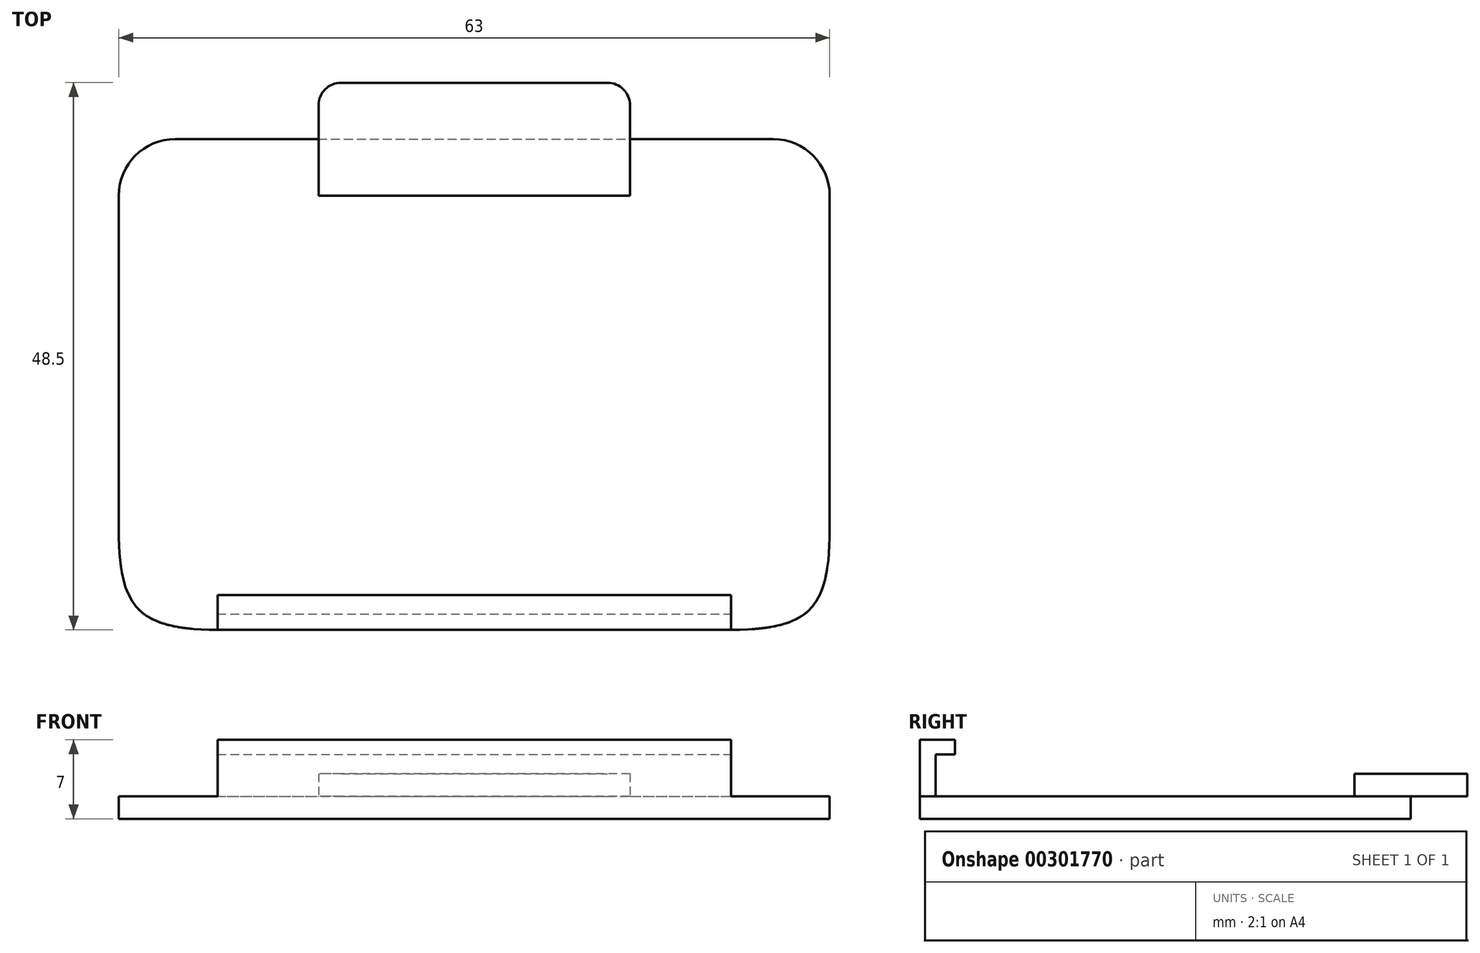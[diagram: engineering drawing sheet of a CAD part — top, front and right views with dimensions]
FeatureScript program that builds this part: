
annotation { "Feature Type Name" : "Feature", "Feature Type Description" : "" }
export const myFeature = defineFeature(function(context is Context, id is Id, definition is map)
    precondition{}
    {
        {
            var Q0;
            Q0=qCreatedBy(makeId("Top.planeOp"),FACE);
            var sketch = newSketch(context, id + "F0", { "sketchPlane" : qUnion([Q0])});
            skLineSegment(sketch, "E0.bottom", {"start": v(-7.54, 4.85) * mm, "end": v(55.46, 4.85) * mm});
            skLineSegment(sketch, "E0.top", {"start": v(-7.54, -38.65) * mm, "end": v(55.46, -38.65) * mm});
            skLineSegment(sketch, "E0.left", {"start": v(-7.54, 4.85) * mm, "end": v(-7.54, -38.65) * mm});
            skLineSegment(sketch, "E0.right", {"start": v(55.46, 4.85) * mm, "end": v(55.46, -38.65) * mm});
            skSolve(sketch);
        }
        {
            var Q0;
            Q0=makeQuery(id+"F0.imprint","IMPRINT",FACE,{"disambiguationData":[TD([[makeQuery(id+"F0.imprint","IMPRINT",EDGE,{"derivedFrom":sQuery(id+"F0.wireOp",EDGE,"E0.bottom")}),-1.0]])]});
            extrude(context, id + "F1", {"entities" : qUnion([Q0]), "depth" : 2 * mm});
        }
        {
            var Q0;
            Q0=makeQuery(id+"F1.opExtrude","SWEPT_EDGE",EDGE,{"disambiguationData":[OSD([sQuery(id+"F0.wireOp",EDGE,"E0.bottom"),sQuery(id+"F0.wireOp",EDGE,"E0.left")])]});
            var Q1;
            Q1=makeQuery(id+"F1.opExtrude","SWEPT_EDGE",EDGE,{"disambiguationData":[OSD([sQuery(id+"F0.wireOp",EDGE,"E0.bottom"),sQuery(id+"F0.wireOp",EDGE,"E0.right")])]});
            fillet(context, id + "F2", {"entities" : qUnion([Q0, Q1]), "radius" : 5 * mm, "tangentPropagation" : true, "allowEdgeOverflow" : false});
        }
        {
            var Q0;
            Q0=makeQuery(id+"F1.opExtrude","CAP_FACE",FACE,{"disambiguationData":[OSD([sQuery(id+"F0.wireOp",EDGE,"E0.bottom"),sQuery(id+"F0.wireOp",EDGE,"E0.top"),sQuery(id+"F0.wireOp",EDGE,"E0.left"),sQuery(id+"F0.wireOp",EDGE,"E0.right")])],"isStart":false});
            var sketch = newSketch(context, id + "F3", { "sketchPlane" : qUnion([Q0])});
            skLineSegment(sketch, "E1", {"start": v(23.96, 4.85) * mm, "end": v(23.96, -38.65) * mm, "construction": true});
            skLineSegment(sketch, "E2", {"start": v(-7.54, -0.15) * mm, "end": v(55.46, -0.15) * mm, "construction": true});
            skLineSegment(sketch, "E3", {"start": v(23.96, -0.15) * mm, "end": v(10.16, -0.15) * mm});
            skLineSegment(sketch, "E4", {"start": v(10.16, -0.15) * mm, "end": v(10.16, 9.85) * mm});
            skLineSegment(sketch, "E5", {"start": v(10.16, 9.85) * mm, "end": v(37.76, 9.85) * mm});
            skLineSegment(sketch, "E6", {"start": v(37.76, 9.85) * mm, "end": v(37.76, -0.15) * mm});
            skLineSegment(sketch, "E7", {"start": v(37.76, -0.15) * mm, "end": v(23.96, -0.15) * mm});
            skLineSegment(sketch, "E8", {"start": v(23.96, -38.65) * mm, "end": v(1.21, -38.65) * mm});
            skLineSegment(sketch, "E9", {"start": v(1.21, -38.65) * mm, "end": v(1.21, -37.25) * mm});
            skLineSegment(sketch, "E10", {"start": v(1.21, -37.25) * mm, "end": v(46.71, -37.25) * mm});
            skLineSegment(sketch, "E11", {"start": v(46.71, -37.25) * mm, "end": v(46.71, -38.65) * mm});
            skLineSegment(sketch, "E12", {"start": v(46.71, -38.65) * mm, "end": v(23.96, -38.65) * mm});
            skSolve(sketch);
        }
        {
            var Q0;
            {var subQ0=sQuery(id+"F3.wireOp",EDGE,"E5");Q0=makeQuery(id+"F3.imprint","IMPRINT",FACE,{"disambiguationData":[TD([[makeQuery(id+"F3.imprint","IMPRINT",EDGE,{"derivedFrom":subQ0}),-1.0]])]});}
            var Q1;
            {var subQ2=sQuery(id+"F3.wireOp",EDGE,"E3");Q1=makeQuery(id+"F3.imprint","IMPRINT",FACE,{"disambiguationData":[TD([[makeQuery(id+"F3.imprint","IMPRINT",EDGE,{"derivedFrom":subQ2}),-1.0]])]});}
            extrude(context, id + "F4", {"entities" : qUnion([Q0, Q1]), "operationType" : NewBodyOperationType.ADD, "depth" : 2 * mm});
        }
        {
            var Q0;
            Q0=makeQuery(id+"F4.opExtrude","SWEPT_EDGE",EDGE,{"disambiguationData":[OSD([sQuery(id+"F3.wireOp",EDGE,"E4"),sQuery(id+"F3.wireOp",EDGE,"E5")])]});
            var Q1;
            Q1=makeQuery(id+"F4.opExtrude","SWEPT_EDGE",EDGE,{"disambiguationData":[OSD([sQuery(id+"F3.wireOp",EDGE,"E5"),sQuery(id+"F3.wireOp",EDGE,"E6")])]});
            fillet(context, id + "F5", {"entities" : qUnion([Q0, Q1]), "radius" : 2 * mm, "tangentPropagation" : true, "allowEdgeOverflow" : false});
        }
        {
            var Q0;
            Q0=makeQuery(id+"F3.imprint","IMPRINT",FACE,{"disambiguationData":[TD([[makeQuery(id+"F3.imprint","IMPRINT",EDGE,{"derivedFrom":sQuery(id+"F3.wireOp",EDGE,"E8")}),1.0]])]});
            extrude(context, id + "F6", {"entities" : qUnion([Q0]), "operationType" : NewBodyOperationType.ADD, "depth" : 5 * mm});
        }
        {
            var Q0;
            Q0=makeQuery(id+"F6.opExtrude","SWEPT_FACE",FACE,{"disambiguationData":[OSD([sQuery(id+"F3.wireOp",EDGE,"E10")])]});
            var sketch = newSketch(context, id + "F7", { "sketchPlane" : qUnion([Q0])});
            skLineSegment(sketch, "E13.bottom", {"start": v(-1.21, 7) * mm, "end": v(-46.71, 7) * mm});
            skLineSegment(sketch, "E13.top", {"start": v(-1.21, 5.7) * mm, "end": v(-46.71, 5.7) * mm});
            skLineSegment(sketch, "E13.left", {"start": v(-1.21, 7) * mm, "end": v(-1.21, 5.7) * mm});
            skLineSegment(sketch, "E13.right", {"start": v(-46.71, 7) * mm, "end": v(-46.71, 5.7) * mm});
            skSolve(sketch);
        }
        {
            var Q0;
            Q0=makeQuery(id+"F7.imprint","IMPRINT",FACE,{"disambiguationData":[TD([[makeQuery(id+"F7.imprint","IMPRINT",EDGE,{"derivedFrom":sQuery(id+"F7.wireOp",EDGE,"E13.bottom")}),1.0]])]});
            extrude(context, id + "F8", {"entities" : qUnion([Q0]), "operationType" : NewBodyOperationType.ADD, "depth" : 1.7 * mm});
        }
        {
            var Q0;
            Q0=makeQuery(id+"F1.opExtrude","SWEPT_EDGE",EDGE,{"disambiguationData":[OSD([sQuery(id+"F0.wireOp",EDGE,"E0.top"),sQuery(id+"F0.wireOp",EDGE,"E0.right")])]});
            var Q1;
            Q1=makeQuery(id+"F1.opExtrude","SWEPT_EDGE",EDGE,{"disambiguationData":[OSD([sQuery(id+"F0.wireOp",EDGE,"E0.top"),sQuery(id+"F0.wireOp",EDGE,"E0.left")])]});
            fillet(context, id + "F9", {"entities" : qUnion([Q0, Q1]), "radius" : 8.93 * mm, "tangentPropagation" : true, "rho" : 0.6, "crossSection" : FilletCrossSection.CONIC, "allowEdgeOverflow" : false});
        }
    });
